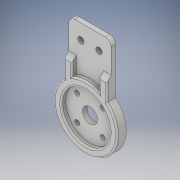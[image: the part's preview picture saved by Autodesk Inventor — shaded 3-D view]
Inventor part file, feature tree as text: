
AUTODESK INVENTOR PART (.ipt)
format: ipt  version: 2018 (Build 220112000, 112)  size: 222,720 bytes
history: native  units: in
note: dims shown in document units (in); Inventor stores cm internally (conversion verified against a paired STEP export)
features: extrude x4, sketch x4, projected_geometry x3, fillet x2, chamfer x1
ambient origin geometry x8: Origin, YZ Plane, XZ Plane, XY Plane, X Axis, Y Axis, Z Axis, Center Point
bodies: Solid1 (feature_tree)
feature tree (14):
  extrude  "Extrusion1"  Depth=1.9685in
  extrude  "Extrusion2"  Depth=1.1024in
  extrude  "Extrusion3"  Depth=0.7874in
  chamfer  "Chamfer1"  Distance=0.1969in
  fillet  "Fillet1"  Radius=0.1181in
  extrude  "Extrusion4"  Depth=0.3937in
  fillet  "Fillet2"  Radius=0.1654in
  sketch  "Sketch1"  dims[d0=1.6535in d1=1.9685in]
  sketch  "Sketch2"  dims[d2=0.1181in d3=0.0in d4=1.1024in]
  projected_geometry  "Projected Loop1"
  sketch  "Sketch3"  dims[d5=1.2598in d6=0.7874in]
  projected_geometry  "Projected Loop2"
  projected_geometry  "Projected Loop3"
  sketch  "Sketch4"  dims[d7=0.1969in d8=0.1969in d9=0.1181in d10=0.0in d11=0.3937in d12=0.1654in d13=0.4724in d14=0.3937in d15=0.1181in d16=0.0in d17=0.1181in d18=0.0787in d19=45.0deg d20=0.0394in d21=45.0deg d22=0.1299in d23=0.4724in d24=1.5748in d26=360.0deg d28=0.1181in d29=0.0in d30=0.1575in]
